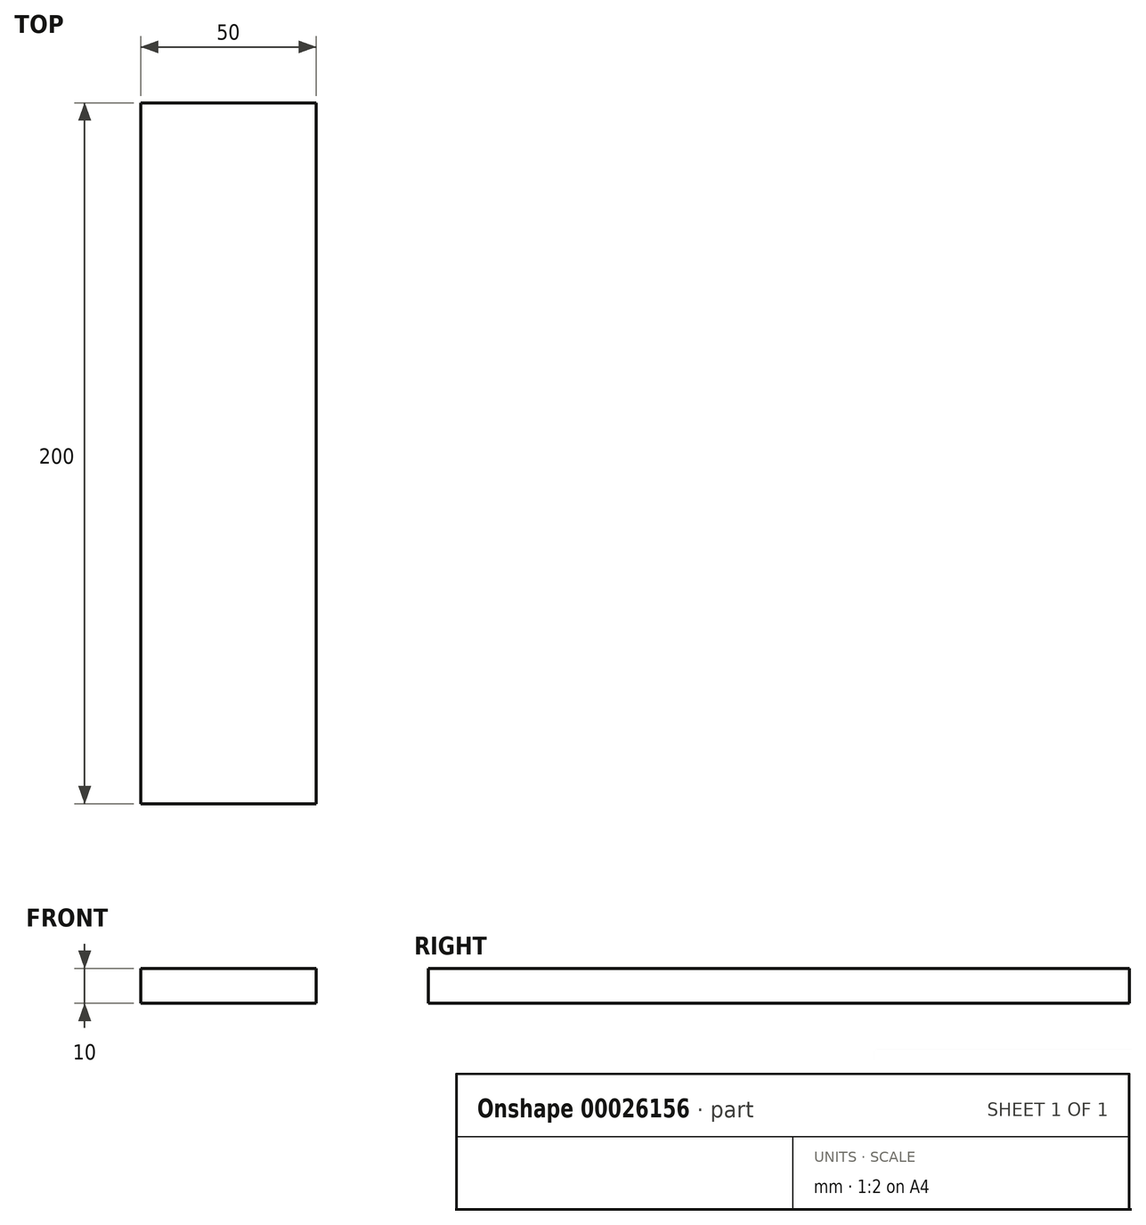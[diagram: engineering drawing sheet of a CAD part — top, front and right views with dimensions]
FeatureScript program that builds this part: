
annotation { "Feature Type Name" : "Feature", "Feature Type Description" : "" }
export const myFeature = defineFeature(function(context is Context, id is Id, definition is map)
    precondition{}
    {
        {
            var Q0;
            Q0=qCreatedBy(makeId("Top.planeOp"),FACE);
            var sketch = newSketch(context, id + "F0", { "sketchPlane" : qUnion([Q0])});
            skLineSegment(sketch, "E0.bottom", {"start": v(-49.8, -44.52) * mm, "end": v(0.2, -44.52) * mm});
            skLineSegment(sketch, "E0.top", {"start": v(-49.8, 155.48) * mm, "end": v(0.2, 155.48) * mm});
            skLineSegment(sketch, "E0.left", {"start": v(-49.8, -44.52) * mm, "end": v(-49.8, 155.48) * mm});
            skLineSegment(sketch, "E0.right", {"start": v(0.2, -44.52) * mm, "end": v(0.2, 155.48) * mm});
            skSolve(sketch);
        }
        {
            var Q0;
            Q0=makeQuery(id+"F0.imprint","IMPRINT",FACE,{"disambiguationData":[TD([[makeQuery(id+"F0.imprint","IMPRINT",EDGE,{"derivedFrom":sQuery(id+"F0.wireOp",EDGE,"E0.bottom")}),1.0]])]});
            extrude(context, id + "F1", {"entities" : qUnion([Q0]), "depth" : 10 * mm});
        }
    });
